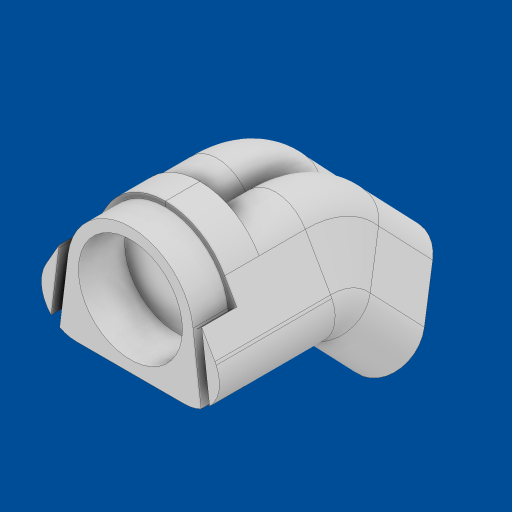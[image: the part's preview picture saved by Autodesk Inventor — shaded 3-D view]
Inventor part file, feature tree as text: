
AUTODESK INVENTOR PART (.ipt)
format: ipt  version: 2023 (Build 270158000, 158)  size: 542,720 bytes
history: native  units: mm
features: extrude x11, sketch x9, plane x3, chamfer x2, mirror x1, revolve x1
ambient origin geometry x8: Origin, YZ Plane, XZ Plane, XY Plane, X Axis, Y Axis, Z Axis, Center Point
bodies: Solid1 (feature_tree)
feature tree (27):
  sketch  "Sketch1"  dims[d0=100.0mm d1=25.0mm d2=7.5mm d3=7.5mm d4=60.0deg d5=15.0mm d6=11.0mm d7=11.0mm d8=15.0mm d14=4.0mm d15=0.0mm]
  extrude  "Extrusion1"  Depth=7.5mm TaperAngle=0.0deg
  plane  "Work Plane13"
  sketch  "Sketch7"  dims[d72=7.5mm d73=90.0deg]
  extrude  "Extrusion6"  TaperAngle=90.0deg  [1 undecoded]
  extrude  "Extrusion7"  Depth=7.5mm
  mirror  "Mirror4"
  plane  "Work Plane9"
  extrude  "Extrusion8"  Depth=15.0mm
  revolve  "Revolution2"  [1 undecoded]
  extrude  "Extrusion9"  Depth=6.5mm
  extrude  "Extrusion10"  Depth=15.0mm TaperAngle=0.0deg
  extrude  "Extrusion11"  Depth=10.0mm TaperAngle=0.0deg
  chamfer  "Chamfer3"  Distance=4.0mm
  chamfer  "Chamfer4"  Distance=10.0mm
  plane  "Work Plane16"
  extrude  "Extrusion14"  Depth=10.0mm TaperAngle=0.0deg
  extrude  "Extrusion21"  Depth=10.0mm TaperAngle=45.0deg
  extrude  "Extrusion25"  Depth=10.0mm TaperAngle=45.0deg
  extrude  "Extrusion28"  Depth=10.0mm
  sketch  "Sketch14"  dims[d74=7.5mm d75=5.5mm]
  sketch  "Sketch15"  dims[d76=5.5mm d77=15.0mm]
  sketch  "Sketch19"  dims[d78=11.0mm d79=11.0mm]
  sketch  "Sketch23"  dims[d80=2.0mm d81=6.5mm]
  sketch  "Sketch24"  dims[d82=6.5mm d83=15.0mm d84=0.0mm]
  sketch  "Sketch34"  dims[d93=10.0mm d94=0.0mm d115=20.0mm d116=0.0mm]
  sketch  "Sketch35"  dims[d131=8.648979mm d132=4.0mm d133=0.0mm d134=10.0mm d135=0.0mm d136=10.0mm d137=0.0mm d138=2.0mm d139=4.0mm d140=45.0deg d141=2.0mm d142=4.0mm d143=45.0deg d153=15.0mm d154=15.0mm d155=15.0mm d156=25.0mm d157=0.0mm d222=45.0mm d243=1.0mm d244=27.222586mm d245=15.0mm d246=0.0mm d266=261.822mm d267=7.45mm d268=27.223mm d269=1.0mm d270=35.0mm d271=100.0mm d272=2.0mm d273=1.1mm d274=180.0deg d275=1.0mm d276=15.709295mm d277=7.55mm d278=0.0mm d279=2.0mm d280=1.0mm d281=180.0deg d301=0.0mm d302=22.5mm d303=10.0mm d304=0.0mm d305=10.0mm d306=5.0mm d182=0.5mm d183=0.872665mm d184=0.5mm d185=0.872665mm d224=0.5mm d225=0.872665mm d226=0.5mm d227=0.872665mm d258=0.5mm d259=0.872665mm d260=0.5mm d261=0.872665mm]
note: 2 required parameter values undecoded (feature->parameter linkage not recoverable at this tier; creation-order binding heuristic only, values carry confidence <= 0.55)